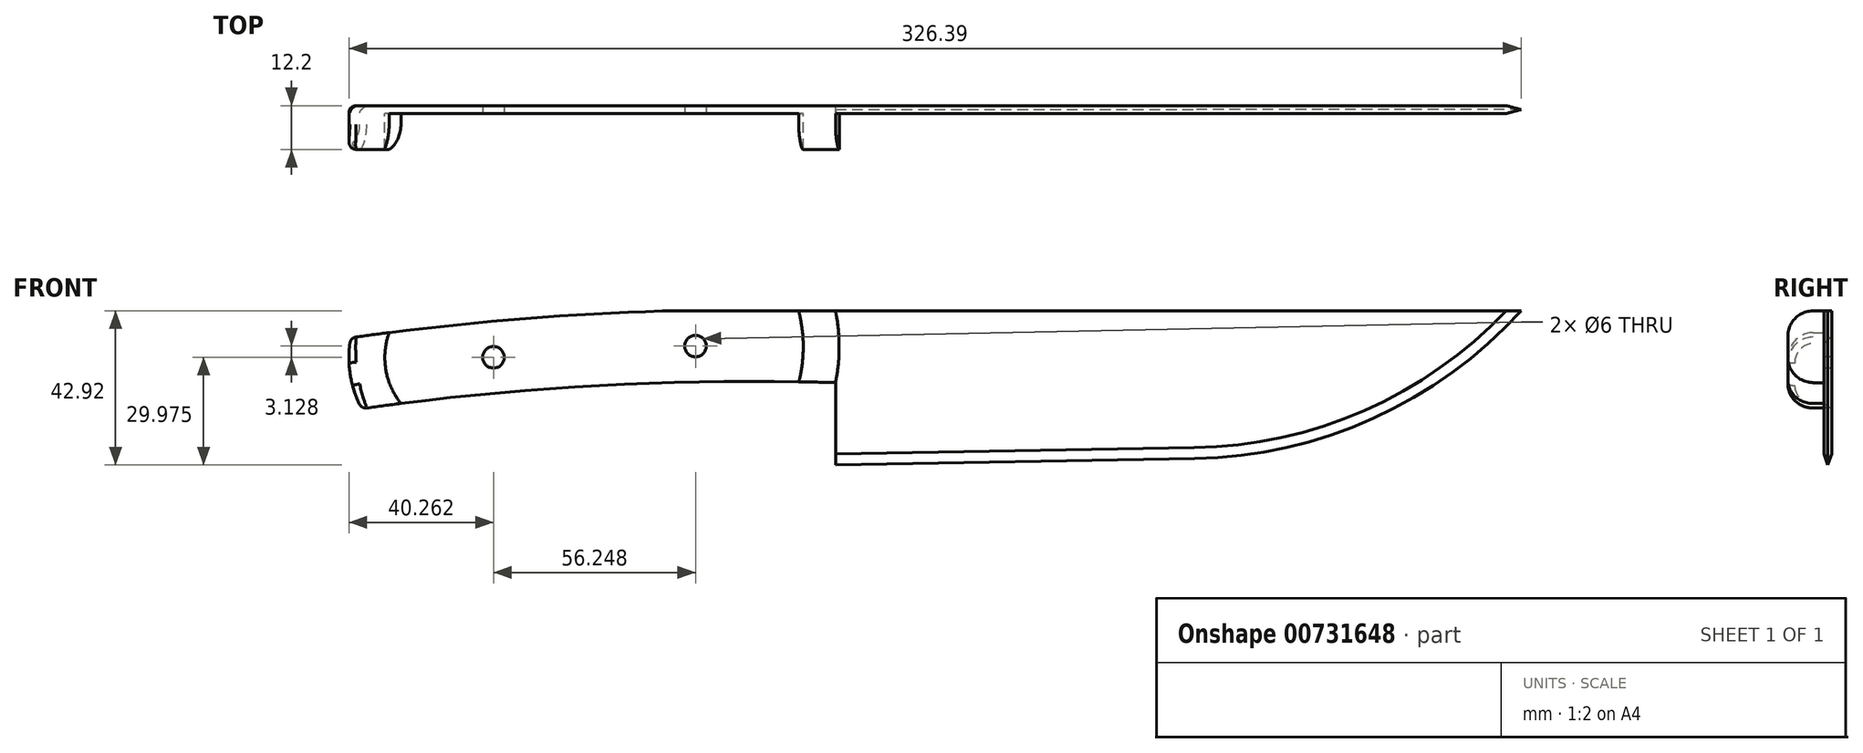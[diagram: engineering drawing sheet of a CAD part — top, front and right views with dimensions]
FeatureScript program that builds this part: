
annotation { "Feature Type Name" : "Feature", "Feature Type Description" : "" }
export const myFeature = defineFeature(function(context is Context, id is Id, definition is map)
    precondition{}
    {
        {
            var Q0;
            Q0=qCreatedBy(makeId("Front.planeOp"),FACE);
            var sketch = newSketch(context, id + "F0", { "sketchPlane" : qUnion([Q0])});
            skLineSegment(sketch, "E0.bottom", {"start": v(-135, -43) * mm, "end": v(191, -43) * mm});
            skLineSegment(sketch, "E0.top", {"start": v(-46.57, 0) * mm, "end": v(191, 0) * mm});
            skLineSegment(sketch, "E0.left", {"start": v(-135, -43) * mm, "end": v(-135, 0) * mm});
            skLineSegment(sketch, "E0.right", {"start": v(191, -43) * mm, "end": v(191, 0) * mm});
            skLineSegment(sketch, "E1", {"start": v(0, 0) * mm, "end": v(0, -43) * mm, "construction": true});
            skLineSegment(sketch, "E2", {"start": v(0, -43) * mm, "end": v(100, -41.25) * mm});
            skArc(sketch, "E3", {"start": v(100, -41.25) * mm, "mid": v(149.77, -30.04) * mm, "end": v(191, 0) * mm});
            skArc(sketch, "E4", {"start": v(0, 0) * mm, "mid": v(-67.66, -0.9) * mm, "end": v(-135, -7.5) * mm});
            skArc(sketch, "E5.0", {"start": v(0, -20) * mm, "mid": v(-66.13, -20.84) * mm, "end": v(-131.96, -27.27) * mm});
            skArc(sketch, "E6", {"start": v(-135, -7.5) * mm, "mid": v(-135.14, -17.64) * mm, "end": v(-131.96, -27.27) * mm});
            skLineSegment(sketch, "E7", {"start": v(0, -43) * mm, "end": v(0, -20) * mm});
            skSolve(sketch);
        }
        {
            var Q0;
            Q0=makeQuery(id+"F0.imprint","IMPRINT",FACE,{"disambiguationData":[TD([[makeQuery(id+"F0.imprint","IMPRINT",EDGE,{"derivedFrom":sQuery(id+"F0.wireOp",EDGE,"E2")}),1.0]])]});
            var Q1;
            {var subQ0=sQuery(id+"F0.wireOp",EDGE,"E6");var subQ1=sQuery(id+"F0.wireOp",EDGE,"E0.left");var subQ3=makeQuery(id+"F0.imprint","INTERSECT",VERTEX,{"derivedFrom":[subQ1,subQ0]});Q1=makeQuery(id+"F0.imprint","IMPRINT",FACE,{"disambiguationData":[TD([[makeQuery(id+"F0.imprint","IMPRINT",EDGE,{"disambiguationData":[TD([[subQ3,-1.0]])],"derivedFrom":subQ1}),1.0]])]});}
            extrude(context, id + "F1", {"entities" : qUnion([Q0, Q1]), "depth" : 1.1 * mm, "offsetDistance" : 25 * mm, "hasSecondDirection" : true, "secondDirectionOppositeDirection" : true, "secondDirectionDepth" : 1.1 * mm});
        }
        {
            var Q0;
            Q0=makeQuery(id+"F1.opExtrude","CAP_FACE",FACE,{"disambiguationData":[OSD([sQuery(id+"F0.wireOp",EDGE,"E0.top"),sQuery(id+"F0.wireOp",EDGE,"E0.left"),sQuery(id+"F0.wireOp",EDGE,"E2"),sQuery(id+"F0.wireOp",EDGE,"E3"),sQuery(id+"F0.wireOp",EDGE,"E4"),sQuery(id+"F0.wireOp",EDGE,"E5.0"),sQuery(id+"F0.wireOp",EDGE,"E6"),sQuery(id+"F0.wireOp",EDGE,"E7")])],"isStart":false});
            var sketch = newSketch(context, id + "F2", { "sketchPlane" : qUnion([Q0])});
            skLineSegment(sketch, "E8.0", {"start": v(-46.57, 0) * mm, "end": v(191, 0) * mm});
            skArc(sketch, "E9.0", {"start": v(0, -20) * mm, "mid": v(-66.13, -20.84) * mm, "end": v(-131.96, -27.27) * mm});
            skArc(sketch, "E10.0", {"start": v(-46.57, 0) * mm, "mid": v(-90.89, -2.52) * mm, "end": v(-135, -7.5) * mm});
            skArc(sketch, "E11.0", {"start": v(-135, -7.5) * mm, "mid": v(-135.14, -17.64) * mm, "end": v(-131.96, -27.27) * mm});
            skArc(sketch, "E12", {"start": v(0, -20) * mm, "mid": v(1.01, -10) * mm, "end": v(0, 0) * mm});
            skArc(sketch, "E13.0", {"start": v(-10.2, -19.77) * mm, "mid": v(-8.99, -9.88) * mm, "end": v(-10.26, 0) * mm});
            skArc(sketch, "E14.0", {"start": v(-124.3, -6.06) * mm, "mid": v(-125.22, -16.36) * mm, "end": v(-121, -25.8) * mm});
            skSolve(sketch);
        }
        {
            var Q0;
            {var subQ0=sQuery(id+"F2.wireOp",EDGE,"E12");Q0=makeQuery(id+"F2.imprint","IMPRINT",FACE,{"disambiguationData":[TD([[makeQuery(id+"F2.imprint","IMPRINT",EDGE,{"derivedFrom":subQ0}),1.0]])]});}
            var Q1;
            {var subQ0=sQuery(id+"F2.wireOp",EDGE,"E11.0");Q1=makeQuery(id+"F2.imprint","IMPRINT",FACE,{"disambiguationData":[TD([[makeQuery(id+"F2.imprint","IMPRINT",EDGE,{"derivedFrom":subQ0}),1.0]])]});}
            extrude(context, id + "F3", {"entities" : qUnion([Q0, Q1]), "operationType" : NewBodyOperationType.ADD, "depth" : 10 * mm, "offsetDistance" : 25 * mm});
        }
        {
            var Q0;
            Q0=makeQuery(id+"F3.opExtrude","CAP_EDGE",EDGE,{"disambiguationData":[OSD([sQuery(id+"F2.wireOp",EDGE,"E10.0")])],"isStart":false});
            var Q1;
            {var subQ0=sQuery(id+"F2.wireOp",EDGE,"E9.0");Q1=makeQuery(id+"F3.opExtrude","CAP_EDGE",EDGE,{"disambiguationData":[OSD([subQ0]),TDD([makeQuery(id+"F2.imprint","IMPRINT",EDGE,{"disambiguationData":[TD([[makeQuery(id+"F2.imprint","INTERSECT",VERTEX,{"derivedFrom":[subQ0,sQuery(id+"F2.wireOp",EDGE,"E11.0")]}),1.0]])],"derivedFrom":subQ0})])],"isStart":false});}
            var Q2;
            Q2=makeQuery(id+"FOhSryVMYCzB9LG_1.1.F3.opExtrude","CAP_EDGE",EDGE,{"disambiguationData":[OSD([sQuery(id+"F2.wireOp",EDGE,"E10.0")])],"isStart":false});
            var Q3;
            {var subQ0=sQuery(id+"F2.wireOp",EDGE,"E9.0");Q3=makeQuery(id+"FOhSryVMYCzB9LG_1.1.F3.opExtrude","CAP_EDGE",EDGE,{"disambiguationData":[OSD([subQ0]),TDD([makeQuery(id+"F2.imprint","IMPRINT",EDGE,{"disambiguationData":[TD([[makeQuery(id+"F2.imprint","INTERSECT",VERTEX,{"derivedFrom":[subQ0,sQuery(id+"F2.wireOp",EDGE,"E11.0")]}),1.0]])],"derivedFrom":subQ0})])],"isStart":false});}
            var Q4;
            Q4=makeQuery(id+"F3.opExtrude","CAP_EDGE",EDGE,{"disambiguationData":[OSD([sQuery(id+"F2.wireOp",EDGE,"E8.0")])],"isStart":false});
            var Q5;
            {var subQ0=sQuery(id+"F2.wireOp",EDGE,"E9.0");Q5=makeQuery(id+"F3.opExtrude","CAP_EDGE",EDGE,{"disambiguationData":[OSD([subQ0]),TDD([makeQuery(id+"F2.imprint","IMPRINT",EDGE,{"disambiguationData":[TD([[makeQuery(id+"F2.imprint","INTERSECT",VERTEX,{"derivedFrom":[subQ0,sQuery(id+"F2.wireOp",EDGE,"E13.0")]}),1.0]])],"derivedFrom":subQ0})])],"isStart":false});}
            var Q6;
            Q6=makeQuery(id+"FOhSryVMYCzB9LG_1.1.F3.opExtrude","CAP_EDGE",EDGE,{"disambiguationData":[OSD([sQuery(id+"F2.wireOp",EDGE,"E8.0")])],"isStart":false});
            var Q7;
            {var subQ0=sQuery(id+"F2.wireOp",EDGE,"E9.0");Q7=makeQuery(id+"FOhSryVMYCzB9LG_1.1.F3.opExtrude","CAP_EDGE",EDGE,{"disambiguationData":[OSD([subQ0]),TDD([makeQuery(id+"F2.imprint","IMPRINT",EDGE,{"disambiguationData":[TD([[makeQuery(id+"F2.imprint","INTERSECT",VERTEX,{"derivedFrom":[subQ0,sQuery(id+"F2.wireOp",EDGE,"E13.0")]}),1.0]])],"derivedFrom":subQ0})])],"isStart":false});}
            fillet(context, id + "F4", {"entities" : qUnion([Q0, Q1, Q2, Q3, Q4, Q5, Q6, Q7]), "radius" : 7 * mm, "tangentPropagation" : true, "allowEdgeOverflow" : false});
        }
        {
            var Q0;
            Q0=makeQuery(id+"F1.opExtrude","SWEPT_EDGE",EDGE,{"disambiguationData":[OSD([sQuery(id+"F0.wireOp",EDGE,"E0.top"),sQuery(id+"F0.wireOp",EDGE,"E4")])]});
            fillet(context, id + "F5", {"entities" : qUnion([Q0]), "radius" : 100 * mm, "tangentPropagation" : true, "allowEdgeOverflow" : false});
        }
        {
            var Q0;
            Q0=makeQuery(id+"F1.opExtrude","CAP_EDGE",EDGE,{"disambiguationData":[OSD([sQuery(id+"F0.wireOp",EDGE,"E2")])],"isStart":false});
            var Q1;
            Q1=makeQuery(id+"F1.opExtrude","CAP_EDGE",EDGE,{"disambiguationData":[OSD([sQuery(id+"F0.wireOp",EDGE,"E2")])],"isStart":true});
            chamfer(context, id + "F6", {"entities" : qUnion([Q0, Q1]), "chamferType" : ChamferType.OFFSET_ANGLE, "width" : 3.1 * mm, "oppositeDirection" : false, "angle" : 20 * degree, "tangentPropagation" : true});
        }
        {
            var Q0;
            {var subQ0=sQuery(id+"F2.wireOp",EDGE,"E11.0");Q0=makeQuery(id+"FOhSryVMYCzB9LG_1.1.F3.boolean.opBoolean","MERGE",FACE,{"derivedFrom":[makeQuery(id+"F3.boolean.opBoolean","MERGE",FACE,{"derivedFrom":[makeQuery(id+"F1.opExtrude","SWEPT_FACE",FACE,{"disambiguationData":[OSD([sQuery(id+"F0.wireOp",EDGE,"E6")])]}),makeQuery(id+"F3.opExtrude","SWEPT_FACE",FACE,{"disambiguationData":[OSD([subQ0])]})]}),makeQuery(id+"FOhSryVMYCzB9LG_1.1.F3.opExtrude","SWEPT_FACE",FACE,{"disambiguationData":[OSD([subQ0])]})]});}
            fillet(context, id + "F7", {"entities" : qUnion([Q0]), "radius" : 2 * mm, "tangentPropagation" : true, "allowEdgeOverflow" : false});
        }
        {
            var Q0;
            {var subQ1=sQuery(id+"F0.wireOp",EDGE,"E5.0");var subQ2=sQuery(id+"F0.wireOp",EDGE,"E4");var subQ4=sQuery(id+"F0.wireOp",EDGE,"E0.top");var subQ6=sQuery(id+"F0.wireOp",EDGE,"E7");Q0=makeQuery(id+"F3.boolean.opBoolean","SPLIT",FACE,{"disambiguationData":[TD([makeQuery(id+"F1.opExtrude","SWEPT_FACE",FACE,{"disambiguationData":[OSD([subQ2])]})])],"derivedFrom":makeQuery(id+"F1.opExtrude","CAP_FACE",FACE,{"disambiguationData":[OSD([subQ4,sQuery(id+"F0.wireOp",EDGE,"E2"),sQuery(id+"F0.wireOp",EDGE,"E3"),subQ2,subQ1,sQuery(id+"F0.wireOp",EDGE,"E6"),subQ6])],"isStart":false})});}
            var sketch = newSketch(context, id + "F8", { "sketchPlane" : qUnion([Q0])});
            skLineSegment(sketch, "E15.0", {"start": v(-45.06, 0) * mm, "end": v(-10.26, 0) * mm});
            skArc(sketch, "E16.0", {"start": v(-48.17, -0.05) * mm, "mid": v(-86.3, -2.15) * mm, "end": v(-124.3, -6.06) * mm});
            skArc(sketch, "E17.0", {"start": v(-45.06, 0) * mm, "mid": v(-46.62, -0.01) * mm, "end": v(-48.17, -0.05) * mm});
            skArc(sketch, "E18.0", {"start": v(-10.2, -19.77) * mm, "mid": v(-65.71, -20.82) * mm, "end": v(-121, -25.8) * mm});
            skCircle(sketch, "E19", {"center": v(-95.24, -12.94) * mm, "radius": 3 * mm});
            skCircle(sketch, "E20", {"center": v(-38.99, -9.82) * mm, "radius": 3 * mm});
            skArc(sketch, "E21.0", {"start": v(-8.99, -9.8) * mm, "mid": v(-67.23, -10.88) * mm, "end": v(-125.24, -16.27) * mm, "construction": true});
            skArc(sketch, "E22.0", {"start": v(-10.2, -19.77) * mm, "mid": v(-8.99, -9.88) * mm, "end": v(-10.26, 0) * mm});
            skArc(sketch, "E23.0", {"start": v(-125.5, -13.28) * mm, "mid": v(-125.24, -16.27) * mm, "end": v(-124.54, -19.2) * mm});
            skArc(sketch, "E24.0", {"start": v(-125.5, -13.28) * mm, "mid": v(-125.22, -9.62) * mm, "end": v(-124.3, -6.06) * mm});
            skArc(sketch, "E25.0", {"start": v(-121, -25.8) * mm, "mid": v(-123.08, -22.67) * mm, "end": v(-124.54, -19.2) * mm});
            skSolve(sketch);
        }
        {
            var Q0;
            Q0=makeQuery(id+"F8.imprint","IMPRINT",FACE,{"disambiguationData":[TD([[makeQuery(id+"F8.imprint","IMPRINT",EDGE,{"derivedFrom":sQuery(id+"F8.wireOp",EDGE,"E19")}),1.0]])]});
            var Q1;
            Q1=makeQuery(id+"F8.imprint","IMPRINT",FACE,{"disambiguationData":[TD([[makeQuery(id+"F8.imprint","IMPRINT",EDGE,{"derivedFrom":sQuery(id+"F8.wireOp",EDGE,"E20")}),1.0]])]});
            extrude(context, id + "F9", {"entities" : qUnion([Q0, Q1]), "operationType" : NewBodyOperationType.REMOVE, "endBound" : BoundingType.THROUGH_ALL, "oppositeDirection" : true, "depth" : 25 * mm, "offsetDistance" : 25 * mm});
        }
    });
